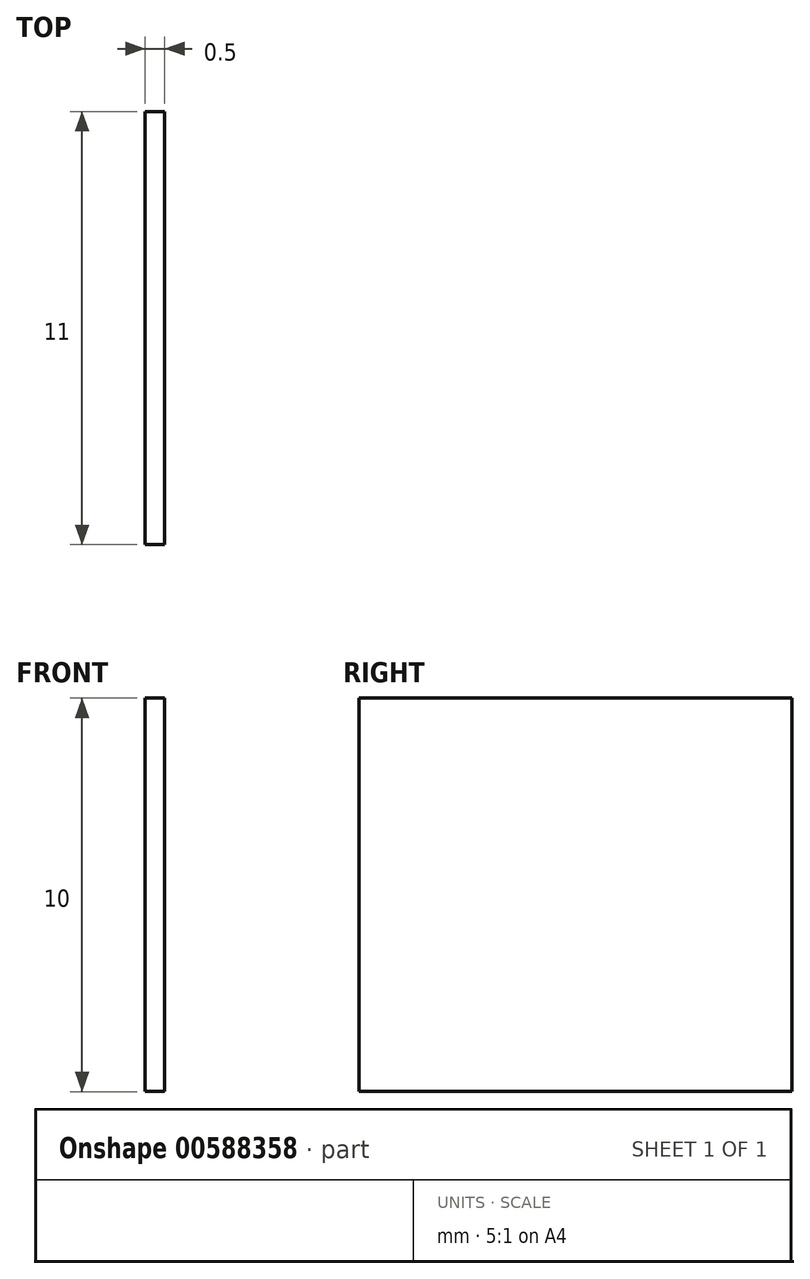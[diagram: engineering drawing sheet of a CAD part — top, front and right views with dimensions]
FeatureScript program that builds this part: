
annotation { "Feature Type Name" : "Feature", "Feature Type Description" : "" }
export const myFeature = defineFeature(function(context is Context, id is Id, definition is map)
    precondition{}
    {
        {
            var Q0;
            Q0=qCreatedBy(makeId("Right.planeOp"),FACE);
            var sketch = newSketch(context, id + "F0", { "sketchPlane" : qUnion([Q0])});
            skLineSegment(sketch, "E0.bottom", {"start": v(-39.52, 38.06) * mm, "end": v(-28.52, 38.06) * mm});
            skLineSegment(sketch, "E0.top", {"start": v(-39.52, 28.06) * mm, "end": v(-28.52, 28.06) * mm});
            skLineSegment(sketch, "E0.left", {"start": v(-39.52, 38.06) * mm, "end": v(-39.52, 28.06) * mm});
            skLineSegment(sketch, "E0.right", {"start": v(-28.52, 38.06) * mm, "end": v(-28.52, 28.06) * mm});
            skLineSegment(sketch, "E1.bottom", {"start": v(-39.52, 38.06) * mm, "end": v(-34.52, 38.06) * mm});
            skLineSegment(sketch, "E1.left", {"start": v(-39.52, 38.06) * mm, "end": v(-39.52, 33.56) * mm});
            skLineSegment(sketch, "E2.bottom", {"start": v(-28.52, 38.06) * mm, "end": v(-33.52, 38.06) * mm});
            skLineSegment(sketch, "E2.left", {"start": v(-28.52, 38.06) * mm, "end": v(-28.52, 33.56) * mm});
            skLineSegment(sketch, "E3.bottom", {"start": v(-39.52, 28.06) * mm, "end": v(-34.52, 28.06) * mm});
            skLineSegment(sketch, "E3.left", {"start": v(-39.52, 28.06) * mm, "end": v(-39.52, 32.56) * mm});
            skLineSegment(sketch, "E4.bottom", {"start": v(-28.52, 28.06) * mm, "end": v(-33.52, 28.06) * mm});
            skLineSegment(sketch, "E4.left", {"start": v(-28.52, 28.06) * mm, "end": v(-28.52, 32.56) * mm});
            skSolve(sketch);
        }
        {
            var Q0;
            Q0=makeQuery(id+"F0.imprint","IMPRINT",FACE,{"disambiguationData":[TD([[makeQuery(id+"F0.imprint","IMPRINT",EDGE,{"derivedFrom":sQuery(id+"F0.wireOp",EDGE,"E0.bottom")}),-1.0]])]});
            extrude(context, id + "F1", {"entities" : qUnion([Q0]), "depth" : .3 * mm, "offsetDistance" : 25 * mm});
        }
        {
            var Q0;
            Q0=makeQuery(id+"F1.opExtrude","CAP_FACE",FACE,{"disambiguationData":[OSD([sQuery(id+"F0.wireOp",EDGE,"E0.bottom"),sQuery(id+"F0.wireOp",EDGE,"E0.top"),sQuery(id+"F0.wireOp",EDGE,"E0.left"),sQuery(id+"F0.wireOp",EDGE,"E0.right"),sQuery(id+"F0.wireOp",EDGE,"E1.bottom"),sQuery(id+"F0.wireOp",EDGE,"E1.left"),sQuery(id+"F0.wireOp",EDGE,"E2.bottom"),sQuery(id+"F0.wireOp",EDGE,"E2.left"),sQuery(id+"F0.wireOp",EDGE,"E3.bottom"),sQuery(id+"F0.wireOp",EDGE,"E3.left"),sQuery(id+"F0.wireOp",EDGE,"E4.bottom"),sQuery(id+"F0.wireOp",EDGE,"E4.left")])],"isStart":false});
            extrude(context, id + "F2", {"entities" : qUnion([Q0]), "operationType" : NewBodyOperationType.ADD, "depth" : .2 * mm, "offsetDistance" : 25 * mm});
        }
    });
